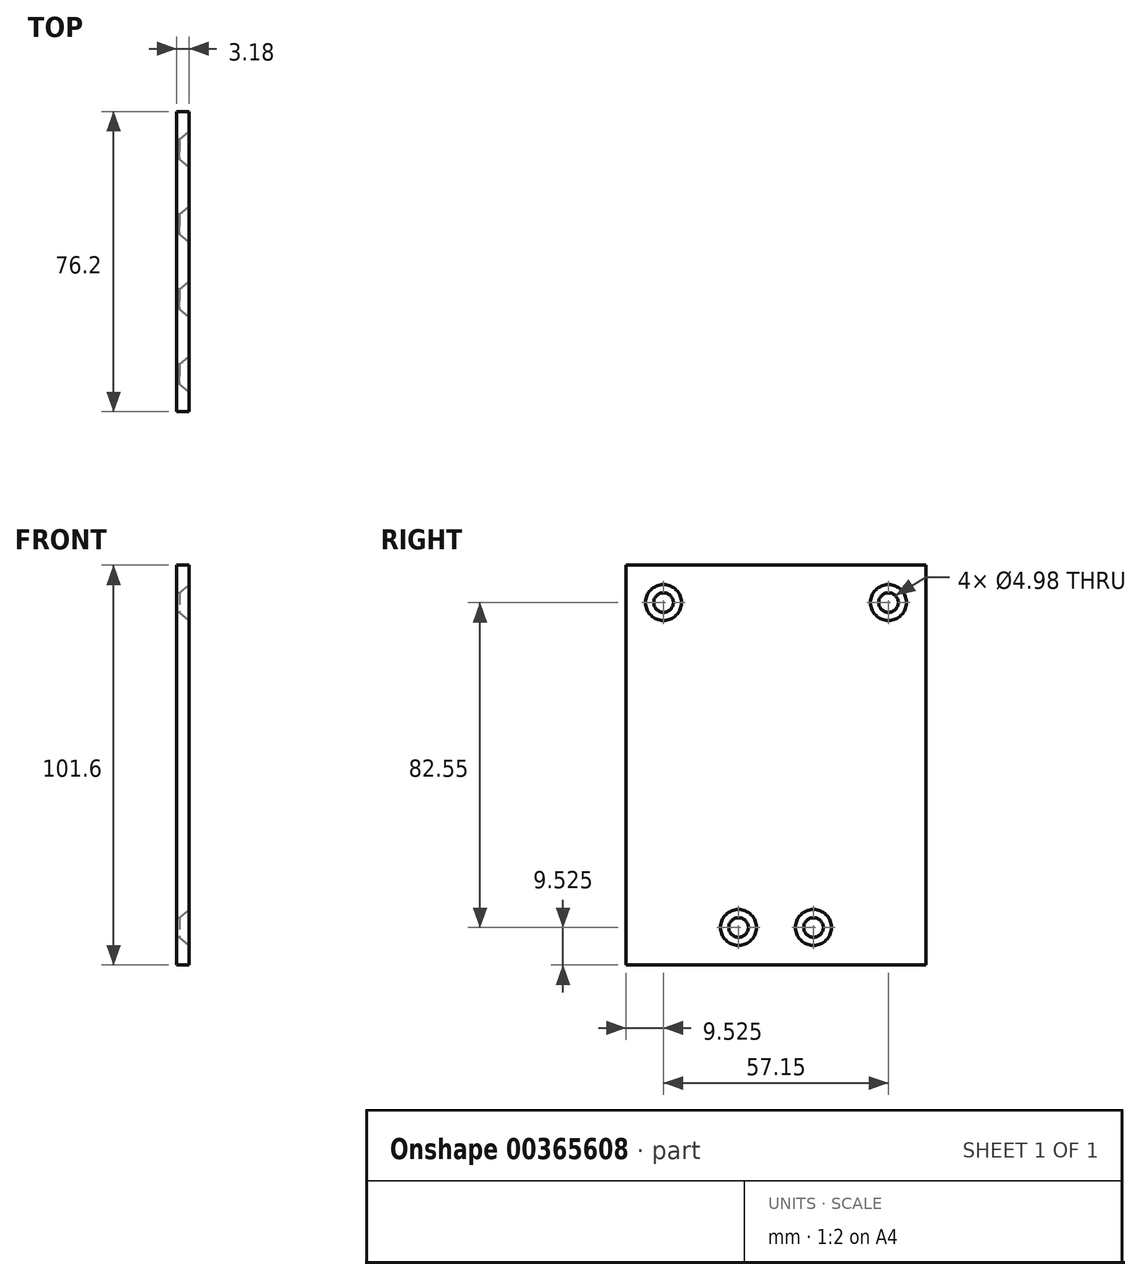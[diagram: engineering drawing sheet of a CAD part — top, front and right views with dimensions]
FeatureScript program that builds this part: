
annotation { "Feature Type Name" : "Feature", "Feature Type Description" : "" }
export const myFeature = defineFeature(function(context is Context, id is Id, definition is map)
    precondition{}
    {
        {
            var Q0;
            Q0=qCreatedBy(makeId("Right.planeOp"),FACE);
            var sketch = newSketch(context, id + "F0", { "sketchPlane" : qUnion([Q0])});
            skLineSegment(sketch, "E0.bottom", {"start": v(38.1, -50.8) * mm, "end": v(-38.1, -50.8) * mm});
            skLineSegment(sketch, "E0.top", {"start": v(38.1, 50.8) * mm, "end": v(-38.1, 50.8) * mm});
            skLineSegment(sketch, "E0.left", {"start": v(38.1, -50.8) * mm, "end": v(38.1, 50.8) * mm});
            skLineSegment(sketch, "E0.right", {"start": v(-38.1, -50.8) * mm, "end": v(-38.1, 50.8) * mm});
            skPoint(sketch, "E0.middle", {"position": v(0, 0) * mm});
            skSolve(sketch);
        }
        {
            var Q0;
            Q0 = qSketchRegion(id + "F0", true);
            extrude(context, id + "F1", {"entities" : qUnion([Q0]), "depth" : 3.17 * mm, "offsetDistance" : 25.4 * mm});
        }
        {
            var Q0;
            Q0=makeQuery(id+"F1.opExtrude","CAP_FACE",FACE,{"disambiguationData":[OSD([sQuery(id+"F0.wireOp",EDGE,"E0.bottom"),sQuery(id+"F0.wireOp",EDGE,"E0.top"),sQuery(id+"F0.wireOp",EDGE,"E0.left"),sQuery(id+"F0.wireOp",EDGE,"E0.right")])],"isStart":false});
            var sketch = newSketch(context, id + "F2", { "sketchPlane" : qUnion([Q0])});
            skPoint(sketch, "E1", {"position": v(-28.58, 41.28) * mm});
            skPoint(sketch, "E2", {"position": v(28.57, 41.28) * mm});
            skPoint(sketch, "E3", {"position": v(9.53, -41.27) * mm});
            skPoint(sketch, "E4", {"position": v(-9.52, -41.27) * mm});
            skSolve(sketch);
        }
        {
            var Q0;
            Q0=sQuery(id+"F2.wireOp",VERTEX,"E1");
            var Q1;
            Q1=sQuery(id+"F2.wireOp",VERTEX,"E2");
            var Q2;
            Q2=sQuery(id+"F2.wireOp",VERTEX,"E3");
            var Q3;
            Q3=sQuery(id+"F2.wireOp",VERTEX,"E4");
            var Q4;
            Q4=makeQuery(id+"F1.opExtrude","SWEPT_BODY",BODY,{"disambiguationData":[OSD([sQuery(id+"F0.wireOp",EDGE,"E0.bottom"),sQuery(id+"F0.wireOp",EDGE,"E0.top"),sQuery(id+"F0.wireOp",EDGE,"E0.left"),sQuery(id+"F0.wireOp",EDGE,"E0.right")])]});
            hole(context, id + "F3", {"style" : HoleStyle.C_SINK, "endStyle" : HoleEndStyle.THROUGH, "standardTappedOrClearance" : lookupTablePath({ "fit" : "Normal (ASME)", "standard" : "ANSI", "size" : "#8", "type" : "Clearance" }), "standardBlindInLast" : lookupTablePath({ "fit" : "Normal", "standard" : "ANSI", "size" : "#8", "type" : "Clearance" }), "holeDiameter" : 4.98 * mm, "cSinkDiameter" : 9.12 * mm, "cSinkAngle" : 82 * degree, "majorDiameter" : 6.35 * mm, "isTappedThrough" : true, "tappedDepth" : 12.7 * mm, "tapClearance" : 3, "locations" : qUnion([Q0, Q1, Q2, Q3]), "scope" : qUnion([Q4]), "startStyle" : HoleStartStyle.SKETCH});
        }
    });
